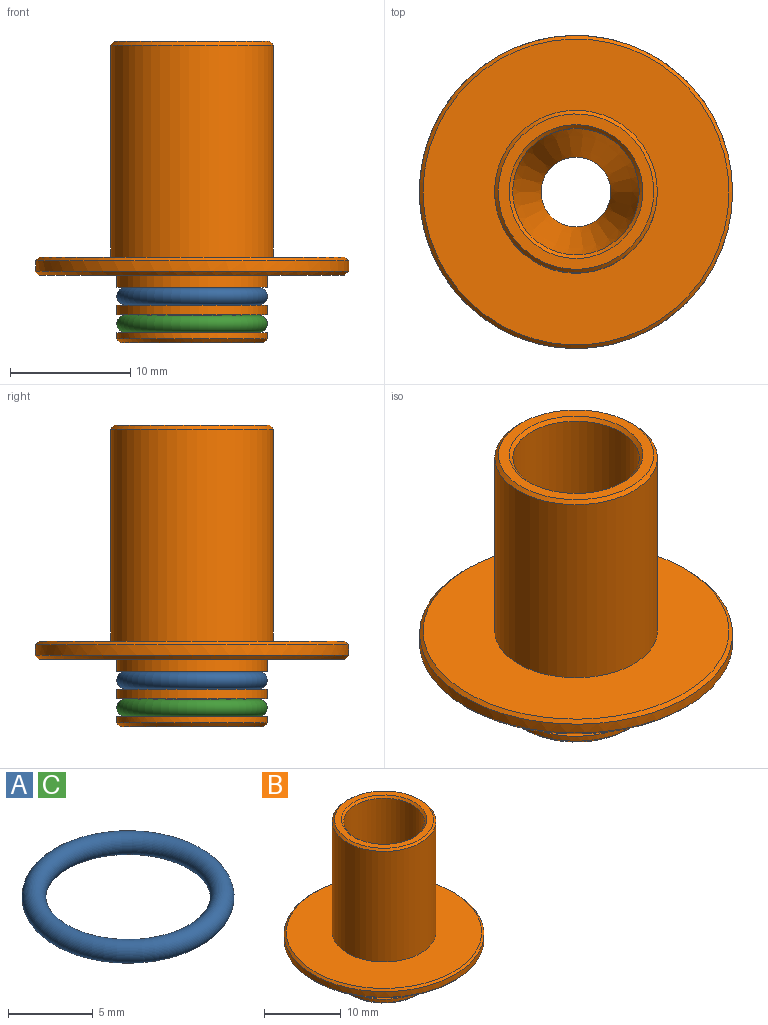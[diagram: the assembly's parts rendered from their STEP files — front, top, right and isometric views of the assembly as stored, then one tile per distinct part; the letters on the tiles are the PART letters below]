
ASSEMBLY  parts=3 mates=2
PART A: 1 faces, bbox 13.5x13.5x1.4 mm
  f0: torus R=5.55mm, axis (0,0,1), area 153.4mm2
PART B: 23 faces, bbox 26x26x25 mm
  f0: plane 12.5x12.5mm, normal (0,0,-1), area 36.1mm2, adj f1,f17
  f1: cylinder r=6.25mm len=12.5mm, axis (0,0,1), area 39.3mm2, adj f0,f2
  f2: plane 25.4x25.4mm, normal (0,0,-1), area 384mm2, adj f1,f18
  f3: cylinder r=13mm len=26mm, axis (0,0,1), area 73.5mm2, adj f18,f19
  f4: plane 25.4x25.4mm, normal (0,0,1), area 363.6mm2, adj f5,f19
  f5: cylinder r=6.75mm len=17.6mm, axis (0,0,1), area 746.4mm2, adj f4,f21
  f6: plane 12.9x12.9mm, normal (0,0,1), area 33.9mm2, adj f21,f22
  f7: cylinder r=5.25mm len=10.5mm, axis (0,0,1), area 340.7mm2, adj f8,f22
  f8: cone r=2.9mm half-angle=15deg, axis (0,0,1), area 232.5mm2, adj f7,f9
  f9: cylinder r=2.9mm len=5.8mm, axis (0,0,1), area 102mm2, adj f8,f10
  f10: plane 11.9x11.9mm, normal (0,0,-1), area 84.8mm2, adj f9,f20
  f11: cylinder r=6.25mm len=12.5mm, axis (0,0,1), area 19.6mm2, adj f12,f20
  f12: plane 12.5x12.5mm, normal (0,0,1), area 36.1mm2, adj f11,f13
  f13: cylinder r=5.25mm len=10.5mm, axis (0,0,1), area 49.5mm2, adj f12,f14
  f14: plane 12.5x12.5mm, normal (0,0,-1), area 36.1mm2, adj f13,f15
  f15: cylinder r=6.25mm len=12.5mm, axis (0,0,1), area 31.4mm2, adj f14,f16
  f16: plane 12.5x12.5mm, normal (0,0,1), area 36.1mm2, adj f15,f17
  f17: cylinder r=5.25mm len=10.5mm, axis (0,0,1), area 49.5mm2, adj f0,f16
  f18: cone r=13mm half-angle=45deg, axis (0,0,1), area 34.3mm2, adj f2,f3
  f19: cone r=12.7mm half-angle=45deg, axis (0,0,-1), area 34.3mm2, adj f3,f4
  f20: cone r=6.25mm half-angle=45deg, axis (0,0,1), area 16.3mm2, adj f10,f11
  f21: cone r=6.45mm half-angle=45deg, axis (0,0,-1), area 17.6mm2, adj f5,f6
  f22: cone r=5.25mm half-angle=45deg, axis (0,0,1), area 14.4mm2, adj f6,f7
PART C: same geometry as A
PLACE A t=(0,0,3.85)mm
PLACE B at identity
PLACE C t=(0,0,1.55)mm
MATE fastened A.f0 <-> B.f1  axis (0,0,1) through (0,0,3.85)mm
MATE fastened C.f0 <-> B.f1  axis (0,0,1) through (0,0,1.55)mm
